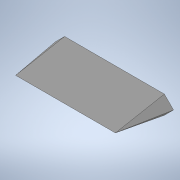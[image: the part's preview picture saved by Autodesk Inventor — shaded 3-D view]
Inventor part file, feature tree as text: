
AUTODESK INVENTOR PART (.ipt)
format: ipt  version: 2020 (Build 240168000, 168)  size: 372,736 bytes
history: native  units: in
note: dims shown in document units (in); Inventor stores cm internally (conversion verified against a paired STEP export)
features: extrude x8, sketch x8, projected_geometry x8, plane x2, mirror x1
ambient origin geometry x8: Origin, YZ Plane, XZ Plane, XY Plane, X Axis, Y Axis, Z Axis, Center Point
bodies: Body1 (feature_tree)
feature tree (27):
  extrude  "Extrusion24"  Depth=3.1496in
  extrude  "Extrusion25"  TaperAngle=0.0deg  [1 undecoded]
  plane  "Work Plane14"
  plane  "Work Plane15"
  extrude  "Extrusion26"  Depth=0.5906in
  extrude  "Extrusion27"  Depth=0.3484in TaperAngle=0.0deg
  mirror  "Mirror11"
  extrude  "Extrusion29"  Depth=5.1181in
  extrude  "Extrusion28"  Depth=0.2756in
  extrude  "Extrusion31"  Depth=0.2362in
  extrude  "Extrusion30"  Depth=0.3937in
  sketch  "Sketch29"  dims[d121=1.1811in d122=3.1496in]
  sketch  "Sketch30"  dims[d123=6.4181in d124=0.0in]
  projected_geometry  "Projected Loop15"
  sketch  "Sketch31"  dims[d125=0.5906in d126=5.6307in]
  sketch  "Sketch32"  dims[d127=0.0in d128=0.3484in d129=0.0in]
  sketch  "Sketch33"  dims[d130=0.9559in d131=0.0in d132=5.1181in]
  sketch  "Sketch34"  dims[d133=0.993in d140=0.2756in]
  projected_geometry  "Projected Loop16"
  sketch  "Sketch36"  dims[d141=0.0in d142=0.2362in]
  projected_geometry  "Projected Loop23"
  projected_geometry  "Projected Loop24"
  sketch  "Sketch37"  dims[d145=0.1496in d149=0.187in d150=0.187in d151=0.3445in d152=0.0in d153=0.3937in d154=-0.3092in d155=0.3937in d156=-0.3092in d158=0.315in d161=0.315in d168=0.1181in d169=0.315in d170=0.315in d50=0.0197in d51=0.0344in d52=0.0197in d53=0.0344in d73=0.0197in d74=0.0344in d75=0.0197in d76=0.0344in]
  projected_geometry  "Projected Loop25"
  projected_geometry  "Projected Loop26"
  projected_geometry  "Projected Loop27"
  projected_geometry  "Projected Loop28"
note: 1 required parameter value undecoded (feature->parameter linkage not recoverable at this tier; creation-order binding heuristic only, values carry confidence <= 0.55)
